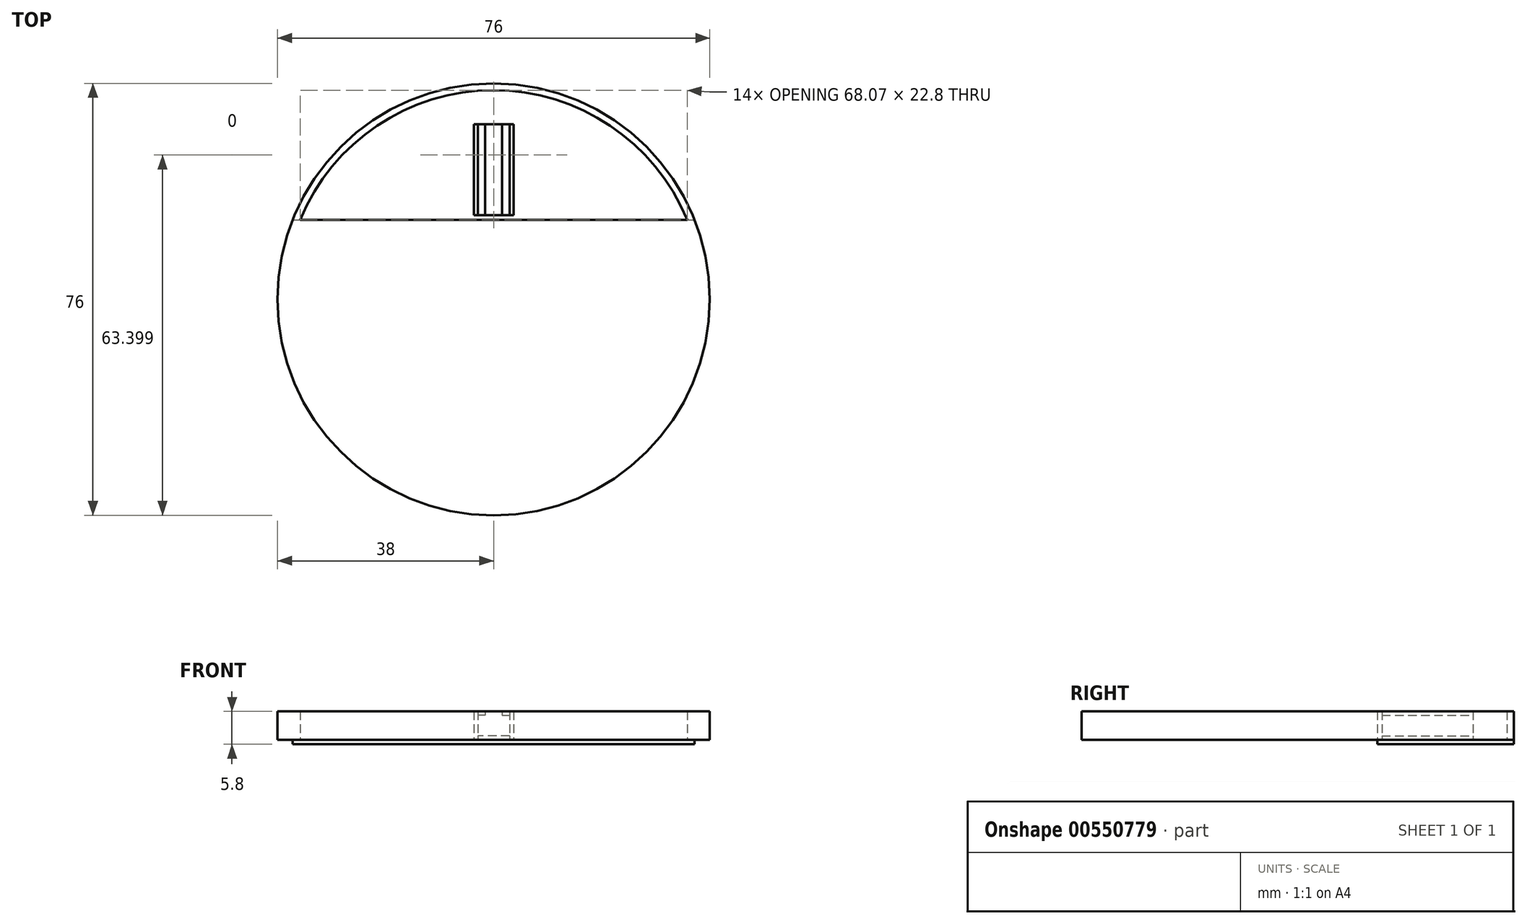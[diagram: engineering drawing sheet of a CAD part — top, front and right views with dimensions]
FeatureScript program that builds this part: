
annotation { "Feature Type Name" : "Feature", "Feature Type Description" : "" }
export const myFeature = defineFeature(function(context is Context, id is Id, definition is map)
    precondition{}
    {
        {
            var Q0;
            Q0=qCreatedBy(makeId("Top.planeOp"),FACE);
            var sketch = newSketch(context, id + "F0", { "sketchPlane" : qUnion([Q0])});
            skCircle(sketch, "E0", {"center": v(0, 0) * mm, "radius": 36.8 * mm});
            skCircle(sketch, "E1.0", {"center": v(0, 0) * mm, "radius": 38 * mm});
            skLineSegment(sketch, "E2", {"start": v(-35, 14.8) * mm, "end": v(35, 14.8) * mm});
            skLineSegment(sketch, "E3.0", {"start": v(-34.6, 14) * mm, "end": v(34.6, 14) * mm});
            skLineSegment(sketch, "E4", {"start": v(0, 14.8) * mm, "end": v(3.5, 14.8) * mm});
            skLineSegment(sketch, "E5", {"start": v(3.5, 14.8) * mm, "end": v(3.5, 30.8) * mm});
            skLineSegment(sketch, "E6", {"start": v(3.5, 30.8) * mm, "end": v(-3.5, 30.8) * mm});
            skLineSegment(sketch, "E7", {"start": v(-3.5, 30.8) * mm, "end": v(-3.5, 14.8) * mm});
            skLineSegment(sketch, "E8.0", {"start": v(-2.8, 30.8) * mm, "end": v(-2.8, 14.8) * mm});
            skLineSegment(sketch, "E9.0", {"start": v(2.8, 14.8) * mm, "end": v(2.8, 30.8) * mm});
            skLineSegment(sketch, "E10", {"start": v(-34.6, 14) * mm, "end": v(-35.33, 14) * mm});
            skLineSegment(sketch, "E11", {"start": v(34.6, 14) * mm, "end": v(35.33, 14) * mm});
            skSolve(sketch);
        }
        {
            var Q0;
            Q0=makeQuery(id+"F0.imprint","IMPRINT",FACE,{"disambiguationData":[TD([[makeQuery(id+"F0.imprint","IMPRINT",EDGE,{"derivedFrom":sQuery(id+"F0.wireOp",EDGE,"E0")}),-1.0]])]});
            var Q1;
            {var subQ0=sQuery(id+"F0.wireOp",EDGE,"E2");var subQ1=sQuery(id+"F0.wireOp",EDGE,"E0");var subQ2=makeQuery(id+"F0.imprint","INTERSECT",VERTEX,{"disambiguationData":[OD(0.0)],"derivedFrom":[subQ1,subQ0]});Q1=makeQuery(id+"F0.imprint","IMPRINT",FACE,{"disambiguationData":[TD([[makeQuery(id+"F0.imprint","IMPRINT",EDGE,{"disambiguationData":[TD([[subQ2,-1.0]])],"derivedFrom":subQ1}),-1.0]])]});}
            var Q2;
            {var subQ0=sQuery(id+"F0.wireOp",EDGE,"E3.0");var subQ1=sQuery(id+"F0.wireOp",EDGE,"E0");var subQ2=makeQuery(id+"F0.imprint","INTERSECT",VERTEX,{"disambiguationData":[OD(0.0)],"derivedFrom":[subQ1,subQ0]});Q2=makeQuery(id+"F0.imprint","IMPRINT",FACE,{"disambiguationData":[TD([[makeQuery(id+"F0.imprint","IMPRINT",EDGE,{"disambiguationData":[TD([[subQ2,-1.0]])],"derivedFrom":subQ1}),1.0]])]});}
            var Q3;
            {var subQ0=sQuery(id+"F0.wireOp",EDGE,"E11");Q3=makeQuery(id+"F0.imprint","IMPRINT",FACE,{"disambiguationData":[TD([[makeQuery(id+"F0.imprint","IMPRINT",EDGE,{"derivedFrom":subQ0}),1.0]])]});}
            var Q4;
            {var subQ0=sQuery(id+"F0.wireOp",EDGE,"E10");Q4=makeQuery(id+"F0.imprint","IMPRINT",FACE,{"disambiguationData":[TD([[makeQuery(id+"F0.imprint","IMPRINT",EDGE,{"derivedFrom":subQ0}),-1.0]])]});}
            var Q5;
            {var subQ4=sQuery(id+"F0.wireOp",EDGE,"E10");Q5=makeQuery(id+"F0.imprint","IMPRINT",FACE,{"disambiguationData":[TD([[makeQuery(id+"F0.imprint","IMPRINT",EDGE,{"derivedFrom":subQ4}),1.0]])]});}
            extrude(context, id + "F1", {"entities" : qUnion([Q0, Q1, Q2, Q3, Q4, Q5]), "depth" : 5 * mm, "offsetDistance" : 25 * mm});
        }
        {
            var Q0;
            {var subQ0=sQuery(id+"F0.wireOp",EDGE,"E5");Q0=makeQuery(id+"F0.imprint","IMPRINT",FACE,{"disambiguationData":[TD([[makeQuery(id+"F0.imprint","IMPRINT",EDGE,{"derivedFrom":subQ0}),-1.0]])]});}
            var Q1;
            {var subQ0=sQuery(id+"F0.wireOp",EDGE,"E2");var subQ1=sQuery(id+"F0.wireOp",EDGE,"E0");var subQ2=makeQuery(id+"F0.imprint","INTERSECT",VERTEX,{"disambiguationData":[OD(0.0)],"derivedFrom":[subQ1,subQ0]});Q1=makeQuery(id+"F0.imprint","IMPRINT",FACE,{"disambiguationData":[TD([[makeQuery(id+"F0.imprint","IMPRINT",EDGE,{"disambiguationData":[TD([[subQ2,-1.0]])],"derivedFrom":subQ1}),-1.0]])]});}
            var Q2;
            {var subQ0=sQuery(id+"F0.wireOp",EDGE,"E2");var subQ2=sQuery(id+"F0.wireOp",EDGE,"E0");var subQ7=makeQuery(id+"F0.imprint","INTERSECT",VERTEX,{"disambiguationData":[OD(0.0)],"derivedFrom":[subQ2,subQ0]});Q2=makeQuery(id+"F0.imprint","IMPRINT",FACE,{"disambiguationData":[TD([[makeQuery(id+"F0.imprint","IMPRINT",EDGE,{"disambiguationData":[TD([[subQ7,1.0]])],"derivedFrom":subQ2}),1.0]])]});}
            var Q3;
            {var subQ0=sQuery(id+"F0.wireOp",EDGE,"E8.0");Q3=makeQuery(id+"F0.imprint","IMPRINT",FACE,{"disambiguationData":[TD([[makeQuery(id+"F0.imprint","IMPRINT",EDGE,{"derivedFrom":subQ0}),1.0]])]});}
            var Q4;
            {var subQ0=sQuery(id+"F0.wireOp",EDGE,"E5");Q4=makeQuery(id+"F0.imprint","IMPRINT",FACE,{"disambiguationData":[TD([[makeQuery(id+"F0.imprint","IMPRINT",EDGE,{"derivedFrom":subQ0}),1.0]])]});}
            var Q5;
            {var subQ0=sQuery(id+"F0.wireOp",EDGE,"E7");Q5=makeQuery(id+"F0.imprint","IMPRINT",FACE,{"disambiguationData":[TD([[makeQuery(id+"F0.imprint","IMPRINT",EDGE,{"derivedFrom":subQ0}),1.0]])]});}
            var Q6;
            {var subQ0=sQuery(id+"F0.wireOp",EDGE,"E11");Q6=makeQuery(id+"F0.imprint","IMPRINT",FACE,{"disambiguationData":[TD([[makeQuery(id+"F0.imprint","IMPRINT",EDGE,{"derivedFrom":subQ0}),1.0]])]});}
            var Q7;
            {var subQ0=sQuery(id+"F0.wireOp",EDGE,"E10");Q7=makeQuery(id+"F0.imprint","IMPRINT",FACE,{"disambiguationData":[TD([[makeQuery(id+"F0.imprint","IMPRINT",EDGE,{"derivedFrom":subQ0}),-1.0]])]});}
            extrude(context, id + "F2", {"entities" : qUnion([Q0, Q1, Q2, Q3, Q4, Q5, Q6, Q7]), "oppositeDirection" : true, "depth" : 0.8 * mm, "offsetDistance" : 25 * mm});
        }
        {
            var Q0;
            {var subQ0=sQuery(id+"F0.wireOp",EDGE,"E8.0");Q0=makeQuery(id+"F0.imprint","IMPRINT",FACE,{"disambiguationData":[TD([[makeQuery(id+"F0.imprint","IMPRINT",EDGE,{"derivedFrom":subQ0}),1.0]])]});}
            extrude(context, id + "F3", {"entities" : qUnion([Q0]), "depth" : 0.7 * mm, "offsetDistance" : 25 * mm});
        }
        {
            var Q0;
            {var subQ0=sQuery(id+"F0.wireOp",EDGE,"E7");Q0=makeQuery(id+"F0.imprint","IMPRINT",FACE,{"disambiguationData":[TD([[makeQuery(id+"F0.imprint","IMPRINT",EDGE,{"derivedFrom":subQ0}),1.0]])]});}
            var Q1;
            {var subQ0=sQuery(id+"F0.wireOp",EDGE,"E5");Q1=makeQuery(id+"F0.imprint","IMPRINT",FACE,{"disambiguationData":[TD([[makeQuery(id+"F0.imprint","IMPRINT",EDGE,{"derivedFrom":subQ0}),1.0]])]});}
            extrude(context, id + "F4", {"entities" : qUnion([Q0, Q1]), "depth" : 5 * mm, "offsetDistance" : 25 * mm});
        }
        {
            var Q0;
            Q0=makeQuery(id+"F4.opExtrude","SWEPT_FACE",FACE,{"disambiguationData":[OSD([sQuery(id+"F0.wireOp",EDGE,"E9.0")])]});
            var sketch = newSketch(context, id + "F5", { "sketchPlane" : qUnion([Q0])});
            skLineSegment(sketch, "E12.0", {"start": v(-14.8, 4.3) * mm, "end": v(-30.8, 4.3) * mm});
            skSolve(sketch);
        }
        {
            var Q0;
            Q0=makeQuery(id+"F4.opExtrude","SWEPT_FACE",FACE,{"disambiguationData":[OSD([sQuery(id+"F0.wireOp",EDGE,"E8.0")])]});
            var sketch = newSketch(context, id + "F6", { "sketchPlane" : qUnion([Q0])});
            skLineSegment(sketch, "E13.0", {"start": v(30.8, 4.3) * mm, "end": v(14.8, 4.3) * mm});
            skSolve(sketch);
        }
        {
            var Q0;
            Q0 = qSketchRegion(id + "F6", true);
            var Q1;
            {var subQ0=sQuery(id+"F5.wireOp",EDGE,"E12.0");Q1=makeQuery(id+"F5.imprint","IMPRINT",FACE,{"disambiguationData":[TD([[makeQuery(id+"F5.imprint","IMPRINT",EDGE,{"derivedFrom":subQ0}),-1.0]])]});}
            extrude(context, id + "F7", {"entities" : qUnion([Q0, Q1]), "depth" : 1.3 * mm, "offsetDistance" : 25 * mm});
        }
        {
            var Q0;
            {var subQ0=sQuery(id+"F6.wireOp",EDGE,"E13.0");Q0=makeQuery(id+"F6.imprint","IMPRINT",FACE,{"disambiguationData":[TD([[makeQuery(id+"F6.imprint","IMPRINT",EDGE,{"derivedFrom":subQ0}),-1.0]])]});}
            extrude(context, id + "F8", {"entities" : qUnion([Q0]), "depth" : 1.3 * mm, "offsetDistance" : 25 * mm});
        }
    });
